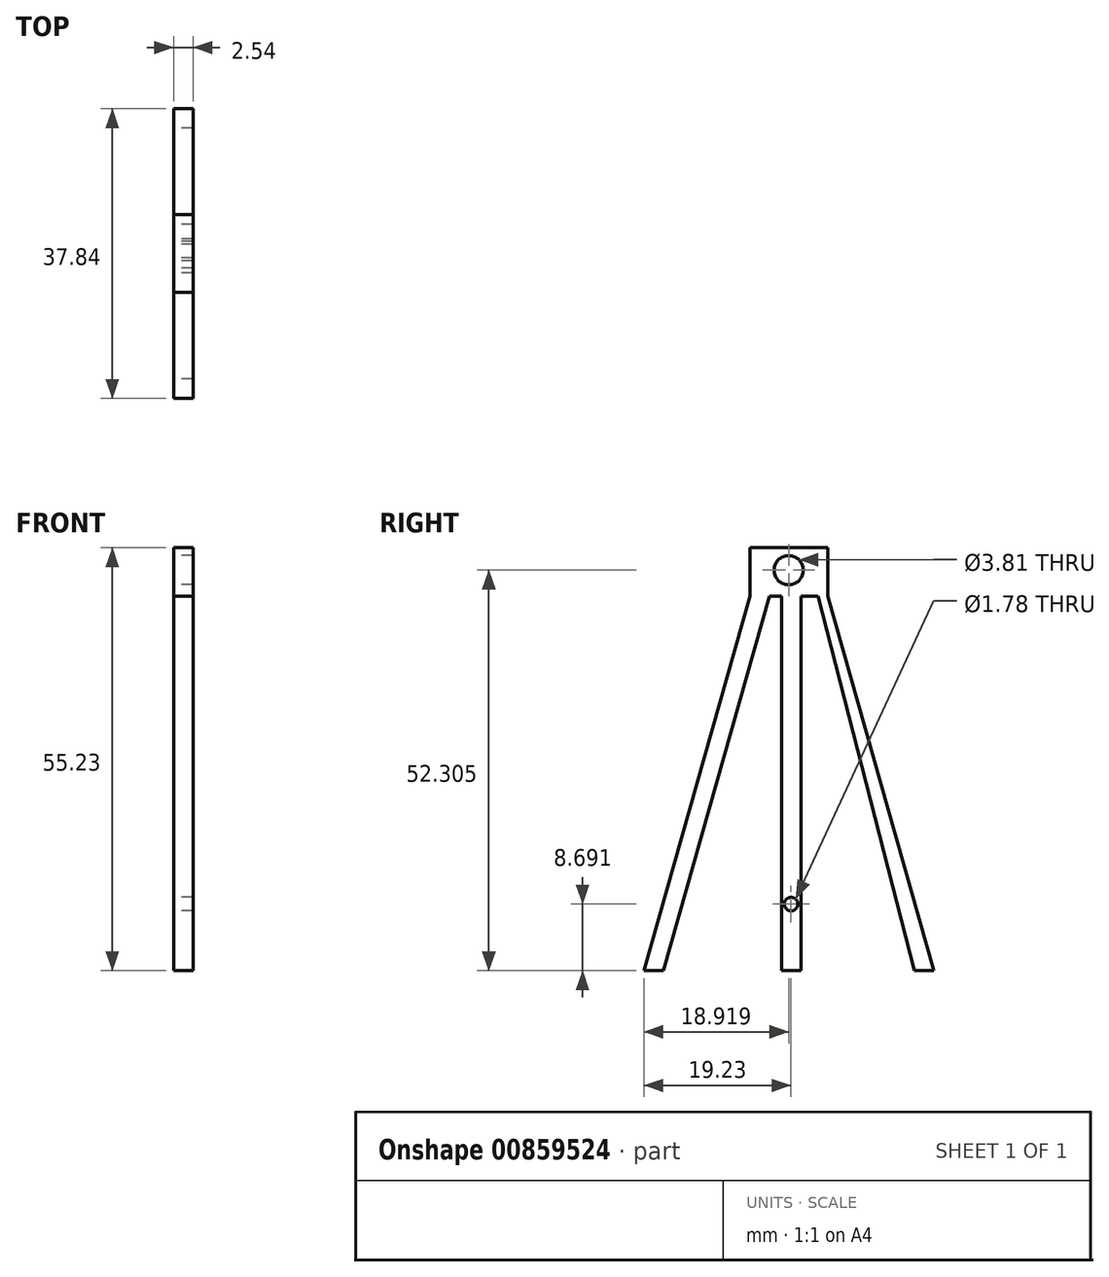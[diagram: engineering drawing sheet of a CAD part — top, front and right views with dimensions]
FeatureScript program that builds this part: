
annotation { "Feature Type Name" : "Feature", "Feature Type Description" : "" }
export const myFeature = defineFeature(function(context is Context, id is Id, definition is map)
    precondition{}
    {
        {
            var Q0;
            Q0=qCreatedBy(makeId("Right.planeOp"),FACE);
            var sketch = newSketch(context, id + "F0", { "sketchPlane" : qUnion([Q0])});
            skLineSegment(sketch, "E0", {"start": v(-1.84, 48.88) * mm, "end": v(12, 0) * mm});
            skLineSegment(sketch, "E1", {"start": v(-1.84, 48.88) * mm, "end": v(-12, 48.88) * mm});
            skLineSegment(sketch, "E2", {"start": v(-12, 48.88) * mm, "end": v(-25.84, 0) * mm});
            skLineSegment(sketch, "E3", {"start": v(-1.84, 48.88) * mm, "end": v(-1.84, 55.23) * mm});
            skLineSegment(sketch, "E4", {"start": v(-1.84, 55.23) * mm, "end": v(-12, 55.23) * mm});
            skLineSegment(sketch, "E5", {"start": v(-12, 55.23) * mm, "end": v(-12, 48.88) * mm});
            skLineSegment(sketch, "E6", {"start": v(-25.84, 0) * mm, "end": v(12, 0) * mm});
            skCircle(sketch, "E7", {"center": v(-6.92, 52.3) * mm, "radius": 1.9 * mm});
            skPoint(sketch, "E7.centerSnap0", {"position": v(-6.92, 48.88) * mm});
            skLineSegment(sketch, "E8", {"start": v(-25.84, 0) * mm, "end": v(-23.3, 0) * mm});
            skLineSegment(sketch, "E9", {"start": v(-23.3, 0) * mm, "end": v(-9.46, 48.88) * mm});
            skLineSegment(sketch, "E10", {"start": v(-3.08, 48.88) * mm, "end": v(9.46, 0) * mm});
            skLineSegment(sketch, "E11", {"start": v(-7.86, 48.88) * mm, "end": v(-7.86, 0) * mm});
            skLineSegment(sketch, "E12", {"start": v(-5.32, 48.88) * mm, "end": v(-5.32, 0) * mm});
            skCircle(sketch, "E13", {"center": v(-6.61, 8.7) * mm, "radius": 0.89 * mm});
            skSolve(sketch);
        }
        {
            var Q0;
            {var subQ0=sQuery(id+"F0.wireOp",EDGE,"E2");Q0=makeQuery(id+"F0.imprint","IMPRINT",FACE,{"disambiguationData":[TD([[makeQuery(id+"F0.imprint","IMPRINT",EDGE,{"derivedFrom":subQ0}),1.0]])]});}
            var Q1;
            {var subQ0=sQuery(id+"F0.wireOp",EDGE,"E3");Q1=makeQuery(id+"F0.imprint","IMPRINT",FACE,{"disambiguationData":[TD([[makeQuery(id+"F0.imprint","IMPRINT",EDGE,{"derivedFrom":subQ0}),1.0]])]});}
            var Q2;
            {var subQ0=sQuery(id+"F0.wireOp",EDGE,"E0");Q2=makeQuery(id+"F0.imprint","IMPRINT",FACE,{"disambiguationData":[TD([[makeQuery(id+"F0.imprint","IMPRINT",EDGE,{"derivedFrom":subQ0}),-1.0]])]});}
            var Q3;
            {var subQ0=sQuery(id+"F0.wireOp",EDGE,"E11");Q3=makeQuery(id+"F0.imprint","IMPRINT",FACE,{"disambiguationData":[TD([[makeQuery(id+"F0.imprint","IMPRINT",EDGE,{"derivedFrom":subQ0}),1.0]])]});}
            extrude(context, id + "F1", {"entities" : qUnion([Q0, Q1, Q2, Q3]), "depth" : 2.54 * mm, "offsetDistance" : 25.4 * mm});
        }
    });
